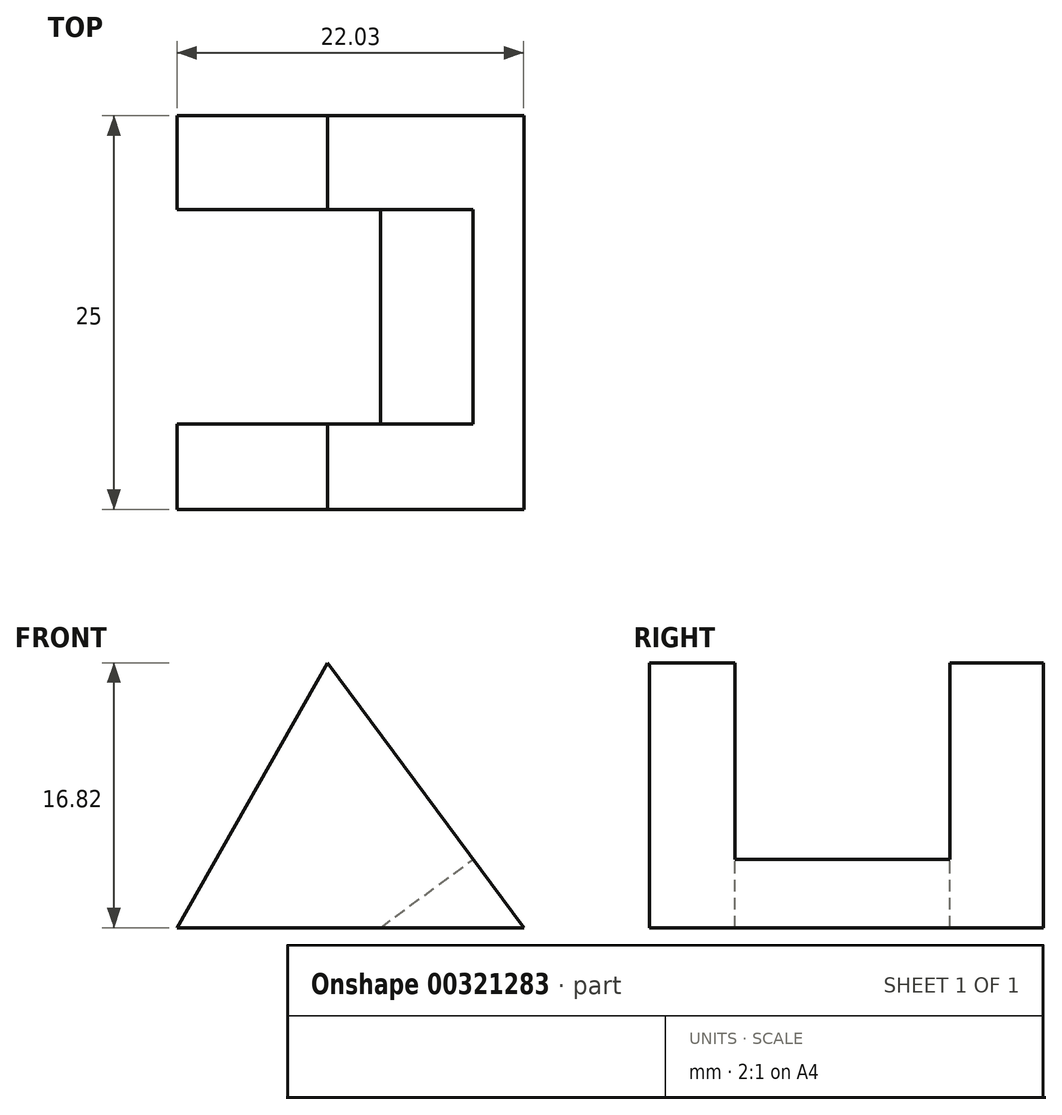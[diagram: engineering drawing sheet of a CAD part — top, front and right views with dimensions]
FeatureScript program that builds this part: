
annotation { "Feature Type Name" : "Feature", "Feature Type Description" : "" }
export const myFeature = defineFeature(function(context is Context, id is Id, definition is map)
    precondition{}
    {
        {
            var Q0;
            Q0=qCreatedBy(makeId("Front.planeOp"),FACE);
            var sketch = newSketch(context, id + "F0", { "sketchPlane" : qUnion([Q0])});
            skLineSegment(sketch, "E0", {"start": v(-40.1, 30.6) * mm, "end": v(-49.66, 13.78) * mm});
            skLineSegment(sketch, "E1", {"start": v(-49.66, 13.78) * mm, "end": v(-27.63, 13.78) * mm});
            skLineSegment(sketch, "E2", {"start": v(-27.63, 13.78) * mm, "end": v(-40.1, 30.6) * mm});
            skSolve(sketch);
        }
        {
            var Q0;
            Q0 = qSketchRegion(id + "F0", true);
            extrude(context, id + "F1", {"entities" : qUnion([Q0]), "oppositeDirection" : true, "depth" : 25 * mm});
        }
        {
            var Q0;
            Q0=makeQuery(id+"F1.opExtrude","SWEPT_FACE",FACE,{"disambiguationData":[OSD([sQuery(id+"F0.wireOp",EDGE,"E2")])]});
            var sketch = newSketch(context, id + "F2", { "sketchPlane" : qUnion([Q0])});
            skLineSegment(sketch, "E3", {"start": v(5.43, 48.46) * mm, "end": v(5.43, 32.94) * mm});
            skLineSegment(sketch, "E4", {"start": v(5.43, 32.94) * mm, "end": v(19.05, 32.94) * mm});
            skLineSegment(sketch, "E5", {"start": v(19.05, 32.94) * mm, "end": v(19.05, 48.46) * mm});
            skSolve(sketch);
        }
        {
            var Q0;
            {var subQ0=sQuery(id+"F2.wireOp",EDGE,"E3");Q0=makeQuery(id+"F2.imprint","IMPRINT",FACE,{"disambiguationData":[TD([[makeQuery(id+"F2.imprint","IMPRINT",EDGE,{"derivedFrom":subQ0}),1.0]])]});}
            extrude(context, id + "F3", {"entities" : qUnion([Q0]), "operationType" : NewBodyOperationType.REMOVE, "oppositeDirection" : true, "depth" : 25 * mm});
        }
        {
            var Q0;
            Q0=qCreatedBy(makeId("Right.planeOp"),FACE);
            var sketch = newSketch(context, id + "F4", { "sketchPlane" : qUnion([Q0])});
            skCircle(sketch, "E6", {"center": v(-33.54, 28.17) * mm, "radius": 3.85 * mm});
            skSolve(sketch);
        }
        {
            var Q0;
            Q0 = qSketchRegion(id + "F4", true);
            extrude(context, id + "F5", {"entities" : qUnion([Q0]), "oppositeDirection" : true, "depth" : 25 * mm});
        }
        {
            var Q0;
            Q0=makeQuery(id+"F5.opExtrude","SWEPT_BODY",BODY,{"disambiguationData":[OSD([sQuery(id+"F4.wireOp",EDGE,"E6")])]});
            deleteBodies(context, id + "F6", {"entities" : qUnion([Q0])});
        }
    });
